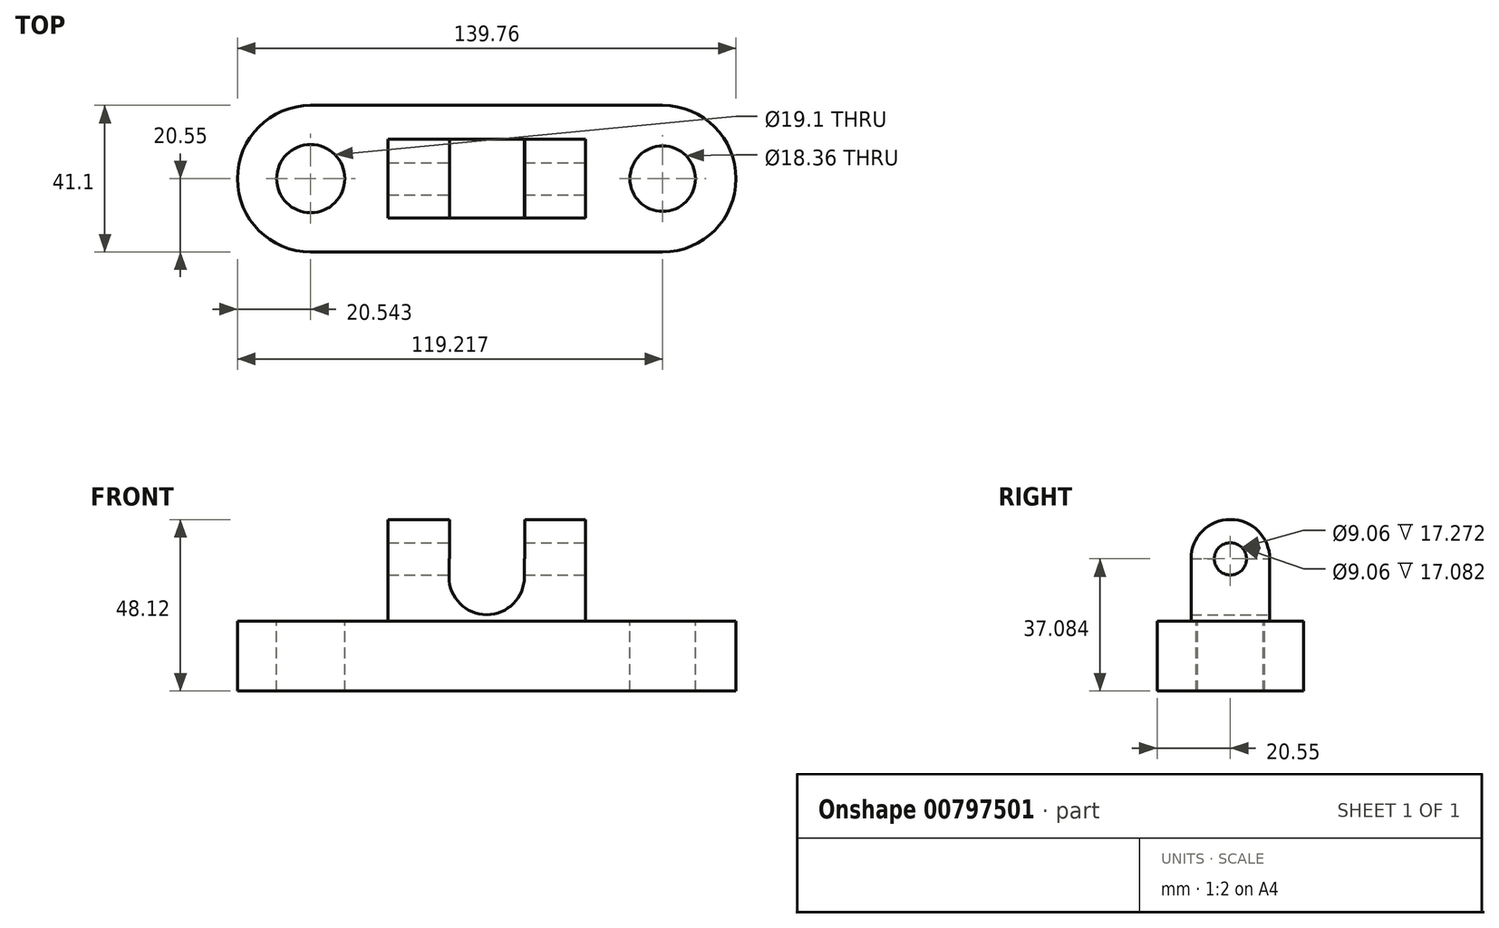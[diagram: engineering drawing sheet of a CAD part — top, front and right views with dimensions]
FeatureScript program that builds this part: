
annotation { "Feature Type Name" : "Feature", "Feature Type Description" : "" }
export const myFeature = defineFeature(function(context is Context, id is Id, definition is map)
    precondition{}
    {
        {
            var Q0;
            Q0=qCreatedBy(makeId("Top.planeOp"),FACE);
            var sketch = newSketch(context, id + "F0", { "sketchPlane" : qUnion([Q0])});
            skLineSegment(sketch, "E0.bottom", {"start": v(49.34, 20.55) * mm, "end": v(-49.34, 20.55) * mm});
            skLineSegment(sketch, "E0.top", {"start": v(49.34, -20.55) * mm, "end": v(-49.34, -20.55) * mm});
            skLineSegment(sketch, "E0.left", {"start": v(49.34, 20.55) * mm, "end": v(49.34, -20.55) * mm});
            skLineSegment(sketch, "E0.right", {"start": v(-49.34, 20.55) * mm, "end": v(-49.34, -20.55) * mm});
            skPoint(sketch, "E0.middle", {"position": v(0, 0) * mm});
            skArc(sketch, "E1", {"start": v(-49.34, 20.55) * mm, "mid": v(-69.88, 0) * mm, "end": v(-49.34, -20.55) * mm});
            skArc(sketch, "E2", {"start": v(49.34, -20.55) * mm, "mid": v(69.88, 0) * mm, "end": v(49.34, 20.55) * mm});
            skSolve(sketch);
        }
        {
            var Q0;
            Q0 = qSketchRegion(id + "F0", true);
            var Q1;
            Q1=makeQuery(id+"F0.imprint","IMPRINT",FACE,{"disambiguationData":[TD([[makeQuery(id+"F0.imprint","IMPRINT",EDGE,{"derivedFrom":sQuery(id+"F0.wireOp",EDGE,"E0.bottom")}),1.0]])]});
            extrude(context, id + "F1", {"entities" : qUnion([Q0, Q1]), "depth" : 19.56 * mm, "offsetDistance" : 25.4 * mm});
        }
        {
            var Q0;
            Q0=makeQuery(id+"F1.opExtrude","CAP_FACE",FACE,{"disambiguationData":[OSD([sQuery(id+"F0.wireOp",EDGE,"E0.bottom"),sQuery(id+"F0.wireOp",EDGE,"E0.top"),sQuery(id+"F0.wireOp",EDGE,"E1"),sQuery(id+"F0.wireOp",EDGE,"E2")])],"isStart":false});
            var sketch = newSketch(context, id + "F2", { "sketchPlane" : qUnion([Q0])});
            skCircle(sketch, "E3", {"center": v(-49.34, 0) * mm, "radius": 9.55 * mm});
            skCircle(sketch, "E4", {"center": v(49.34, 0) * mm, "radius": 9.18 * mm});
            skSolve(sketch);
        }
        {
            var Q0;
            Q0=makeQuery(id+"F2.imprint","IMPRINT",FACE,{"disambiguationData":[TD([[makeQuery(id+"F2.imprint","IMPRINT",EDGE,{"derivedFrom":sQuery(id+"F2.wireOp",EDGE,"E4")}),1.0]])]});
            var Q1;
            Q1=makeQuery(id+"F2.imprint","IMPRINT",FACE,{"disambiguationData":[TD([[makeQuery(id+"F2.imprint","IMPRINT",EDGE,{"derivedFrom":sQuery(id+"F2.wireOp",EDGE,"E3")}),1.0]])]});
            extrude(context, id + "F3", {"entities" : qUnion([Q0, Q1]), "operationType" : NewBodyOperationType.REMOVE, "oppositeDirection" : true, "depth" : 38.35 * mm, "offsetDistance" : 25.4 * mm});
        }
        {
            var Q0;
            Q0=makeQuery(id+"F1.opExtrude","CAP_FACE",FACE,{"disambiguationData":[OSD([sQuery(id+"F0.wireOp",EDGE,"E0.bottom"),sQuery(id+"F0.wireOp",EDGE,"E0.top"),sQuery(id+"F0.wireOp",EDGE,"E1"),sQuery(id+"F0.wireOp",EDGE,"E2")])],"isStart":false});
            var sketch = newSketch(context, id + "F4", { "sketchPlane" : qUnion([Q0])});
            skLineSegment(sketch, "E5.bottom", {"start": v(27.66, 11.04) * mm, "end": v(-27.66, 11.04) * mm});
            skLineSegment(sketch, "E5.top", {"start": v(27.66, -11.04) * mm, "end": v(-27.66, -11.04) * mm});
            skLineSegment(sketch, "E5.left", {"start": v(27.66, 11.04) * mm, "end": v(27.66, -11.04) * mm});
            skLineSegment(sketch, "E5.right", {"start": v(-27.66, 11.04) * mm, "end": v(-27.66, -11.04) * mm});
            skPoint(sketch, "E5.middle", {"position": v(0, 0) * mm});
            skSolve(sketch);
        }
        {
            var Q0;
            Q0 = qSketchRegion(id + "F4", true);
            var Q1;
            Q1=makeQuery(id+"F4.imprint","IMPRINT",FACE,{"disambiguationData":[TD([[makeQuery(id+"F4.imprint","IMPRINT",EDGE,{"derivedFrom":sQuery(id+"F4.wireOp",EDGE,"E5.bottom")}),1.0]])]});
            extrude(context, id + "F5", {"entities" : qUnion([Q0, Q1]), "operationType" : NewBodyOperationType.ADD, "depth" : 17.53 * mm, "offsetDistance" : 25.4 * mm});
        }
        {
            var Q0;
            Q0=makeQuery(id+"F5.opExtrude","CAP_FACE",FACE,{"disambiguationData":[OSD([sQuery(id+"F4.wireOp",EDGE,"E5.bottom"),sQuery(id+"F4.wireOp",EDGE,"E5.top"),sQuery(id+"F4.wireOp",EDGE,"E5.left"),sQuery(id+"F4.wireOp",EDGE,"E5.right")])],"isStart":false});
            var sketch = newSketch(context, id + "F6", { "sketchPlane" : qUnion([Q0])});
            skLineSegment(sketch, "E6.bottom", {"start": v(-10.57, -11.04) * mm, "end": v(10.57, -11.04) * mm});
            skLineSegment(sketch, "E6.top", {"start": v(-10.57, 11.04) * mm, "end": v(10.57, 11.04) * mm});
            skLineSegment(sketch, "E6.left", {"start": v(-10.57, -11.04) * mm, "end": v(-10.57, 11.04) * mm});
            skLineSegment(sketch, "E6.right", {"start": v(10.57, -11.04) * mm, "end": v(10.57, 11.04) * mm});
            skPoint(sketch, "E6.middle", {"position": v(0, 0) * mm});
            skSolve(sketch);
        }
        {
            var Q0;
            Q0=makeQuery(id+"F6.imprint","IMPRINT",FACE,{"disambiguationData":[TD([[makeQuery(id+"F6.imprint","IMPRINT",EDGE,{"derivedFrom":sQuery(id+"F6.wireOp",EDGE,"E6.bottom")}),-1.0]])]});
            extrude(context, id + "F7", {"entities" : qUnion([Q0]), "operationType" : NewBodyOperationType.REMOVE, "oppositeDirection" : true, "depth" : 5.08 * mm, "offsetDistance" : 25.4 * mm});
        }
        {
            var Q0;
            Q0=makeQuery(id+"F5.opExtrude","SWEPT_FACE",FACE,{"disambiguationData":[OSD([sQuery(id+"F4.wireOp",EDGE,"E5.bottom")])]});
            var sketch = newSketch(context, id + "F8", { "sketchPlane" : qUnion([Q0])});
            skArc(sketch, "E7", {"start": v(-10.57, 32) * mm, "mid": v(0, 21.43) * mm, "end": v(10.57, 32) * mm});
            skSolve(sketch);
        }
        {
            var Q0;
            Q0 = qSketchRegion(id + "F8", true);
            var Q1;
            Q1=makeQuery(id+"F8.imprint","IMPRINT",FACE,{"disambiguationData":[TD([[makeQuery(id+"F8.imprint","IMPRINT",EDGE,{"derivedFrom":sQuery(id+"F8.wireOp",EDGE,"E7")}),1.0]])]});
            extrude(context, id + "F9", {"entities" : qUnion([Q0, Q1]), "operationType" : NewBodyOperationType.REMOVE, "oppositeDirection" : true, "depth" : 159.77 * mm, "offsetDistance" : 25.4 * mm});
        }
        {
            var Q0;
            Q0=makeQuery(id+"F5.opExtrude","SWEPT_FACE",FACE,{"disambiguationData":[OSD([sQuery(id+"F4.wireOp",EDGE,"E5.left")])]});
            var sketch = newSketch(context, id + "F10", { "sketchPlane" : qUnion([Q0])});
            skArc(sketch, "E8", {"start": v(11.04, 37.08) * mm, "mid": v(0, 48.12) * mm, "end": v(-11.04, 37.08) * mm});
            skSolve(sketch);
        }
        {
            var Q0;
            Q0 = qSketchRegion(id + "F10", true);
            var Q1;
            Q1=makeQuery(id+"F10.imprint","IMPRINT",FACE,{"disambiguationData":[TD([[makeQuery(id+"F10.imprint","IMPRINT",EDGE,{"derivedFrom":sQuery(id+"F10.wireOp",EDGE,"E8")}),1.0]])]});
            extrude(context, id + "F11", {"entities" : qUnion([Q0, Q1]), "operationType" : NewBodyOperationType.ADD, "oppositeDirection" : true, "depth" : 17.02 * mm, "offsetDistance" : 25.4 * mm});
        }
        {
            var Q0;
            Q0=makeQuery(id+"F5.opExtrude","SWEPT_FACE",FACE,{"disambiguationData":[OSD([sQuery(id+"F4.wireOp",EDGE,"E5.right")])]});
            var sketch = newSketch(context, id + "F12", { "sketchPlane" : qUnion([Q0])});
            skArc(sketch, "E9", {"start": v(11.04, 37.08) * mm, "mid": v(0, 48.12) * mm, "end": v(-11.04, 37.08) * mm});
            skSolve(sketch);
        }
        {
            var Q0;
            Q0 = qSketchRegion(id + "F12", true);
            var Q1;
            Q1=makeQuery(id+"F12.imprint","IMPRINT",FACE,{"disambiguationData":[TD([[makeQuery(id+"F12.imprint","IMPRINT",EDGE,{"derivedFrom":sQuery(id+"F12.wireOp",EDGE,"E9")}),1.0]])]});
            extrude(context, id + "F13", {"entities" : qUnion([Q0, Q1]), "operationType" : NewBodyOperationType.ADD, "oppositeDirection" : true, "depth" : 17.27 * mm, "offsetDistance" : 25.4 * mm});
        }
        {
            var Q0;
            {var subQ0=sQuery(id+"F4.wireOp",EDGE,"E5.left");Q0=makeQuery(id+"F11.boolean.opBoolean","MERGE",FACE,{"derivedFrom":[makeQuery(id+"F5.opExtrude","SWEPT_FACE",FACE,{"disambiguationData":[OSD([subQ0])]}),makeQuery(id+"F11.opExtrude","CAP_FACE",FACE,{"disambiguationData":[OSD([subQ0,sQuery(id+"F10.wireOp",EDGE,"E8")])],"isStart":true})]});}
            var sketch = newSketch(context, id + "F14", { "sketchPlane" : qUnion([Q0])});
            skCircle(sketch, "E10", {"center": v(0, 37.08) * mm, "radius": 4.53 * mm});
            skSolve(sketch);
        }
        {
            var Q0;
            Q0=makeQuery(id+"F14.imprint","IMPRINT",FACE,{"disambiguationData":[TD([[makeQuery(id+"F14.imprint","IMPRINT",EDGE,{"derivedFrom":sQuery(id+"F14.wireOp",EDGE,"E10")}),1.0]])]});
            extrude(context, id + "F15", {"entities" : qUnion([Q0]), "operationType" : NewBodyOperationType.REMOVE, "oppositeDirection" : true, "depth" : 118.87 * mm, "offsetDistance" : 25.4 * mm});
        }
    });
